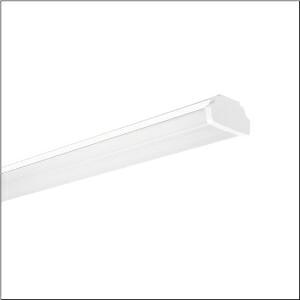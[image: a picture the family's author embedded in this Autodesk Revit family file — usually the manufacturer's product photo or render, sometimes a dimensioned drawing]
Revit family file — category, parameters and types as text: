
# Revit family: modario_r__31_mo_53bm812d2v6085_42f2
name_source: partatom
category: Lighting Fixtures
units: mm (PartAtom-declared; Revit-internal decimal feet)

## family parameters
Cut with Voids When Loaded = No
Host = Face
Light Source = No
Part Type = Normal
Room Calculation Point = No
Round Connector Dimension = Use Diameter
Shared = No

## types (1)
- --- (1 x LED, 8960 lm, 61.8 W, 6500K)
    Apparent Load = 62 VA
    CIE Flux Codes = 47 80 95 92 100
    Color Rendering = 80
    Color Temperature = 6500K
    Default Elevation = 1800 mm
    Description = Modario® 31 MO, luminaire insert, of sheet steel, coil coated, white, length: 1.495mm, width: 81mm, height: 82mm, 5x system unit, system units: 299mm, LED rated luminous flux: 8.960lm, light colour: 865, control gear: DALI 2, control gear: ECG DALI, with plug, 5-pole, with phase selection, mains connection: 220..240V, AC, 50/60Hz, rated input power: 62W, through-wiring accessed according to module size, primary optical cover: cover, of PMMA, light emission: direct distribution, primary light characteristic: symmetric, protection rating (complete): IP20, protection rating (LED compartment): IP50, insulation class (complete): insulation class I (protective earthing), certification: CE, ENEC, VDE, UKCA, impact resistance: IK03, permissible ambient temperature for indoor applications: -25..+30°C, corresponds to IFS (International Featured Standards) requirements for safety and quality in the food industry, reducing of maximum allowable ambient temperature of 5°C with ceiling mounting, packaging unit: 1 piece
    Height = 92 mm
    Lamp = 1 x LED
    Lamp Light Flux = 8960 lm
    Lamp Power = 61.8 W
    Lamp count = 1
    Length = 1495 mm
    Luminous efficacy = 145 lm/W
    Manufacturer = Siteco
    ModVariant = No
    Model = 53BM812D2V6085
    Mounting Place = Ceiling
    Mounting Type = Pendant
    Number of Poles = 1
    OnlyDefault = Yes
    Power Factor = 1
    Product Name = Modario® 31 MO
    Product group = luminaire insert
    ProductGroupID = 901
    Protection Class = Protection class I
    Protection Degree = IP 20
    RLX_Detail_Level = 1
    RLX_Emergency_Light_Flux = 0 lm
    RLX_Emergency_Type = 0
    RLX_Emergency_Type_DB = No
    RlxData = <blob elided: 42293 chars, md5=eadcbdf6>
    Socket = socket
    Standby Power = 0 W
    System Light Flux = 8960 lm
    System Power = 62 W
    Type Comments = factory setting: luminous flux: 100 % | dim-lin: 254 | 500 mA
    Type Image = l_1300283.jpg
    URL = http://relux.com
    VarID = @adj_148741
    Voltage = 0 V
    Weight = 0.00 kg
    Width = 81 mm

## geometry (parser evidence)
native form markers: Blend x4, Sweep x13
no freeform markers — native parametric forms only
